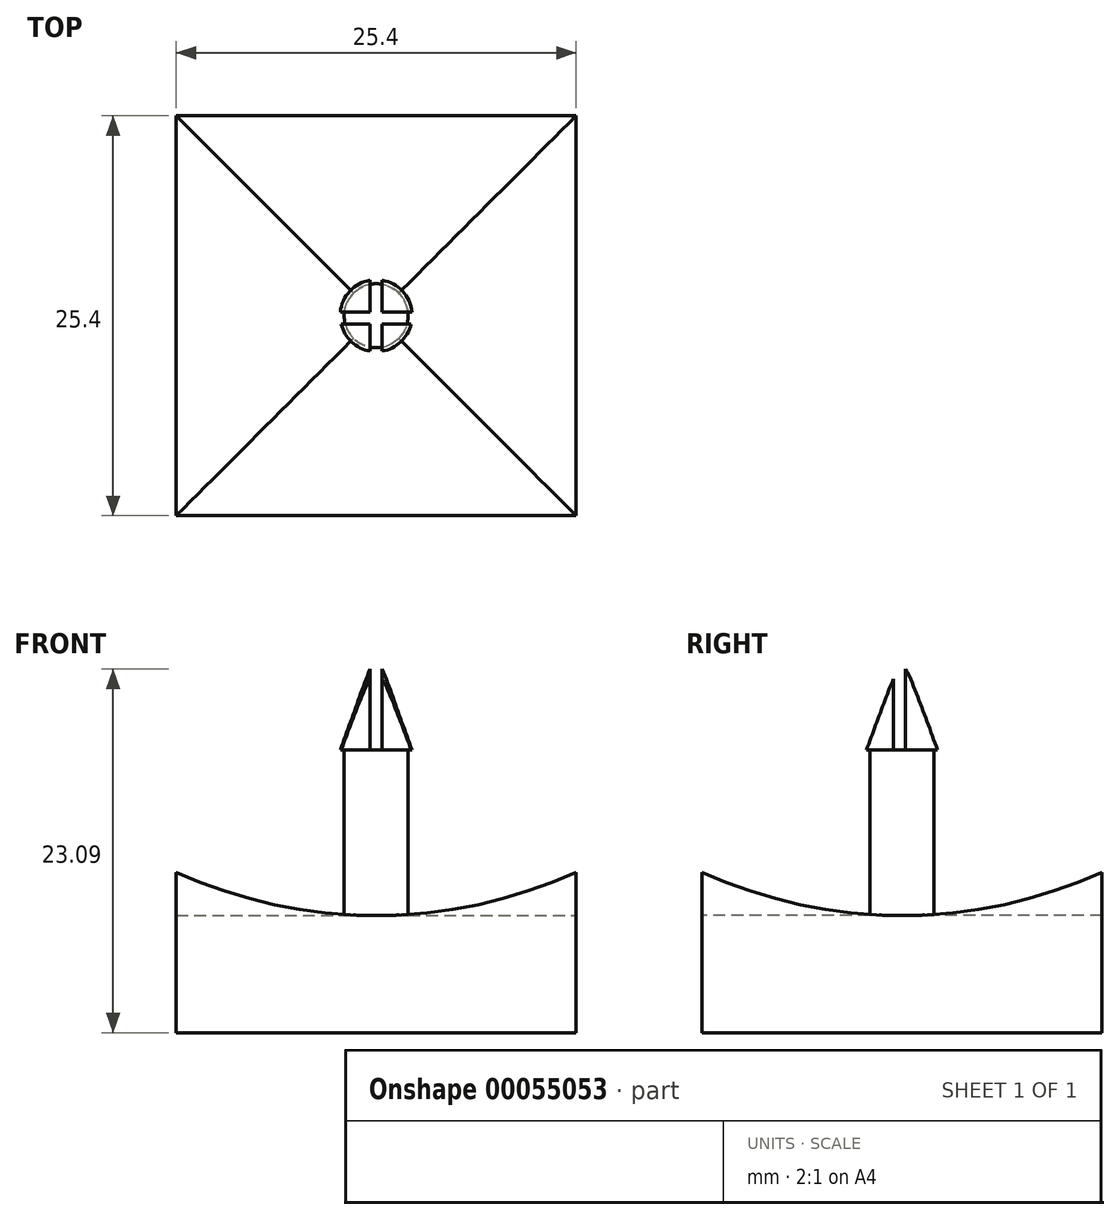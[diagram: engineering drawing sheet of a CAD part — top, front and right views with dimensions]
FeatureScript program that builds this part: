
annotation { "Feature Type Name" : "Feature", "Feature Type Description" : "" }
export const myFeature = defineFeature(function(context is Context, id is Id, definition is map)
    precondition{}
    {
        {
            var Q0;
            Q0=qCreatedBy(makeId("Top.planeOp"),FACE);
            var sketch = newSketch(context, id + "F0", { "sketchPlane" : qUnion([Q0])});
            skLineSegment(sketch, "E0.bottom", {"start": v(-12.7, 12.7) * mm, "end": v(12.7, 12.7) * mm});
            skLineSegment(sketch, "E0.top", {"start": v(-12.7, -12.7) * mm, "end": v(12.7, -12.7) * mm});
            skLineSegment(sketch, "E0.left", {"start": v(-12.7, 12.7) * mm, "end": v(-12.7, -12.7) * mm});
            skLineSegment(sketch, "E0.right", {"start": v(12.7, 12.7) * mm, "end": v(12.7, -12.7) * mm});
            skLineSegment(sketch, "E1", {"start": v(0, 12.7) * mm, "end": v(0, -12.7) * mm});
            skLineSegment(sketch, "E2", {"start": v(12.7, 0) * mm, "end": v(-12.7, 0) * mm});
            skPoint(sketch, "E3", {"position": v(0, 0) * mm});
            skSolve(sketch);
        }
        {
            var Q0;
            Q0 = qSketchRegion(id + "F0", true);
            extrude(context, id + "F1", {"entities" : qUnion([Q0]), "depth" : 12.7 * mm});
        }
        {
            var Q0;
            Q0=makeQuery(id+"F1.opExtrude","SWEPT_FACE",FACE,{"disambiguationData":[OSD([sQuery(id+"F0.wireOp",EDGE,"E0.top")])]});
            var sketch = newSketch(context, id + "F2", { "sketchPlane" : qUnion([Q0])});
            skLineSegment(sketch, "E4.bottom", {"start": v(-12.7, 0) * mm, "end": v(12.7, 0) * mm});
            skLineSegment(sketch, "E4.top", {"start": v(-12.7, 38.1) * mm, "end": v(12.7, 38.1) * mm});
            skLineSegment(sketch, "E4.left", {"start": v(-12.7, 0) * mm, "end": v(-12.7, 38.1) * mm});
            skLineSegment(sketch, "E4.right", {"start": v(12.7, 0) * mm, "end": v(12.7, 38.1) * mm});
            skPoint(sketch, "E5", {"position": v(0, 38.1) * mm});
            skCircle(sketch, "E6", {"center": v(0, 38.1) * mm, "radius": 30.66 * mm});
            skPoint(sketch, "E7", {"position": v(-12.7, 10.2) * mm});
            skSolve(sketch);
        }
        {
            var Q0;
            {var subQ3=sQuery(id+"F2.wireOp",EDGE,"E4.top");Q0=makeQuery(id+"F2.imprint","IMPRINT",FACE,{"disambiguationData":[TD([[makeQuery(id+"F2.imprint","IMPRINT",EDGE,{"derivedFrom":subQ3}),1.0]])]});}
            var Q1;
            {var subQ0=sQuery(id+"F2.wireOp",EDGE,"E4.top");Q1=makeQuery(id+"F2.imprint","IMPRINT",FACE,{"disambiguationData":[TD([[makeQuery(id+"F2.imprint","IMPRINT",EDGE,{"derivedFrom":subQ0}),-1.0]])]});}
            var Q2;
            {var subQ1=makeQuery(id+"F1.opExtrude","CAP_EDGE",EDGE,{"disambiguationData":[OSD([sQuery(id+"F0.wireOp",EDGE,"E0.top")])],"isStart":false});Q2=makeQuery(id+"F2.imprint","IMPRINT",FACE,{"disambiguationData":[TD([[makeQuery(id+"F2.imprint","IMPRINT",EDGE,{"derivedFrom":subQ1}),-1.0]])]});}
            extrude(context, id + "F3", {"entities" : qUnion([Q0, Q1, Q2]), "operationType" : NewBodyOperationType.REMOVE, "oppositeDirection" : true, "depth" : 25.4 * mm});
        }
        {
            var Q0;
            Q0=makeQuery(id+"F1.opExtrude","SWEPT_FACE",FACE,{"disambiguationData":[OSD([sQuery(id+"F0.wireOp",EDGE,"E0.right")])]});
            var sketch = newSketch(context, id + "F4", { "sketchPlane" : qUnion([Q0])});
            skLineSegment(sketch, "E8.bottom", {"start": v(-12.7, 0) * mm, "end": v(12.7, 0) * mm});
            skLineSegment(sketch, "E8.top", {"start": v(-12.7, 38.1) * mm, "end": v(12.7, 38.1) * mm});
            skLineSegment(sketch, "E8.left", {"start": v(-12.7, 0) * mm, "end": v(-12.7, 38.1) * mm});
            skLineSegment(sketch, "E8.right", {"start": v(12.7, 0) * mm, "end": v(12.7, 38.1) * mm});
            skPoint(sketch, "E9", {"position": v(0, 38.1) * mm});
            skCircle(sketch, "E10", {"center": v(0, 38.1) * mm, "radius": 30.66 * mm});
            skLineSegment(sketch, "E11", {"start": v(-12.7, 10.2) * mm, "end": v(0, 38.1) * mm});
            skLineSegment(sketch, "E12", {"start": v(12.7, 10.2) * mm, "end": v(0, 38.1) * mm});
            skLineSegment(sketch, "E13", {"start": v(0, 7.44) * mm, "end": v(0, 0) * mm});
            skSolve(sketch);
        }
        {
            var Q0;
            {var subQ0=sQuery(id+"F4.wireOp",EDGE,"E8.top");Q0=makeQuery(id+"F4.imprint","IMPRINT",FACE,{"disambiguationData":[TD([[makeQuery(id+"F4.imprint","IMPRINT",EDGE,{"derivedFrom":subQ0}),-1.0]])]});}
            var Q1;
            {var subQ1=makeQuery(id+"F3.boolean.opBoolean","INTERSECT",EDGE,{"derivedFrom":[makeQuery(id+"F1.opExtrude","SWEPT_FACE",FACE,{"disambiguationData":[OSD([sQuery(id+"F0.wireOp",EDGE,"E0.right")])]}),makeQuery(id+"F3.opExtrude","SWEPT_FACE",FACE,{"disambiguationData":[OSD([sQuery(id+"F2.wireOp",EDGE,"E6")])]})]});Q1=makeQuery(id+"F4.imprint","IMPRINT",FACE,{"disambiguationData":[TD([[makeQuery(id+"F4.imprint","IMPRINT",EDGE,{"derivedFrom":subQ1}),-1.0]])]});}
            extrude(context, id + "F5", {"entities" : qUnion([Q0, Q1]), "operationType" : NewBodyOperationType.REMOVE, "oppositeDirection" : true, "depth" : 25.4 * mm});
        }
        {
            var Q0;
            Q0=makeQuery(id+"F1.opExtrude","CAP_FACE",FACE,{"disambiguationData":[OSD([sQuery(id+"F0.wireOp",EDGE,"E0.bottom"),sQuery(id+"F0.wireOp",EDGE,"E0.top"),sQuery(id+"F0.wireOp",EDGE,"E0.left"),sQuery(id+"F0.wireOp",EDGE,"E0.right")])],"isStart":true});
            cPlane(context, id + "F6", {"entities" : qUnion([Q0]), "cplaneType" : CPlaneType.OFFSET, "offset" : 5.26 * mm, "oppositeDirection" : true, "width" : 152.4 * mm, "height" : 152.4 * mm});
        }
        {
            var Q0;
            Q0=makeQuery(id+"F1.opExtrude","SWEPT_FACE",FACE,{"disambiguationData":[OSD([sQuery(id+"F0.wireOp",EDGE,"E0.top")])]});
            cPlane(context, id + "F7", {"entities" : qUnion([Q0]), "cplaneType" : CPlaneType.OFFSET, "offset" : 12.7 * mm, "oppositeDirection" : true, "width" : 152.4 * mm, "height" : 152.4 * mm});
        }
        {
            var Q0;
            Q0=qCreatedBy(id+"F6.planeOp",FACE);
            var sketch = newSketch(context, id + "F8", { "sketchPlane" : qUnion([Q0])});
            skPoint(sketch, "E14", {"position": v(0, 0) * mm});
            skSolve(sketch);
        }
        {
            var Q0;
            Q0=qCreatedBy(id+"F7.planeOp",FACE);
            var sketch = newSketch(context, id + "F9", { "sketchPlane" : qUnion([Q0])});
            skPoint(sketch, "E15", {"position": v(0, 5.26) * mm});
            skLineSegment(sketch, "E16.bottom", {"start": v(2.03, 5.26) * mm, "end": v(0, 5.26) * mm});
            skLineSegment(sketch, "E16.top", {"start": v(2.03, 17.96) * mm, "end": v(0, 17.96) * mm});
            skLineSegment(sketch, "E16.left", {"start": v(2.03, 5.26) * mm, "end": v(2.03, 17.96) * mm});
            skLineSegment(sketch, "E16.right", {"start": v(0, 5.26) * mm, "end": v(0, 17.96) * mm});
            skLineSegment(sketch, "E17", {"start": v(0, 17.96) * mm, "end": v(0, 24.3) * mm});
            skLineSegment(sketch, "E18", {"start": v(0, 24.3) * mm, "end": v(2.29, 17.96) * mm});
            skLineSegment(sketch, "E19", {"start": v(2.29, 17.96) * mm, "end": v(2.03, 17.96) * mm});
            skSolve(sketch);
        }
        {
            var Q0;
            Q0=makeQuery(id+"F1.opExtrude","CAP_FACE",FACE,{"disambiguationData":[OSD([sQuery(id+"F0.wireOp",EDGE,"E0.bottom"),sQuery(id+"F0.wireOp",EDGE,"E0.top"),sQuery(id+"F0.wireOp",EDGE,"E0.left"),sQuery(id+"F0.wireOp",EDGE,"E0.right")])],"isStart":true});
            cPlane(context, id + "F10", {"entities" : qUnion([Q0]), "cplaneType" : CPlaneType.OFFSET, "offset" : 24.3 * mm, "oppositeDirection" : true, "width" : 152.4 * mm, "height" : 152.4 * mm});
        }
        {
            var Q0;
            Q0=qCreatedBy(id+"F10.planeOp",FACE);
            var sketch = newSketch(context, id + "F11", { "sketchPlane" : qUnion([Q0])});
            skPoint(sketch, "E20", {"position": v(0, 0) * mm});
            skLineSegment(sketch, "E21.bottom", {"start": v(0.38, 2.29) * mm, "end": v(-0.38, 2.29) * mm});
            skLineSegment(sketch, "E21.top", {"start": v(0.38, -2.29) * mm, "end": v(-0.38, -2.29) * mm});
            skLineSegment(sketch, "E21.left", {"start": v(0.38, 2.29) * mm, "end": v(0.38, -2.29) * mm});
            skLineSegment(sketch, "E21.right", {"start": v(-0.38, 2.29) * mm, "end": v(-0.38, -2.29) * mm});
            skLineSegment(sketch, "E22", {"start": v(0.38, 0) * mm, "end": v(-0.38, 0) * mm});
            skLineSegment(sketch, "E23.bottom", {"start": v(-2.29, -0.22) * mm, "end": v(2.29, -0.22) * mm});
            skLineSegment(sketch, "E23.top", {"start": v(-2.29, 0.54) * mm, "end": v(2.29, 0.54) * mm});
            skLineSegment(sketch, "E23.left", {"start": v(-2.29, -0.22) * mm, "end": v(-2.29, 0.54) * mm});
            skLineSegment(sketch, "E23.right", {"start": v(2.29, -0.22) * mm, "end": v(2.29, 0.54) * mm});
            skLineSegment(sketch, "E24", {"start": v(0, 0.54) * mm, "end": v(0, -0.22) * mm});
            skSolve(sketch);
        }
        {
            var Q0;
            Q0=makeQuery(id+"F9.imprint","IMPRINT",FACE,{"disambiguationData":[TD([[makeQuery(id+"F9.imprint","IMPRINT",EDGE,{"derivedFrom":sQuery(id+"F9.wireOp",EDGE,"E16.top")}),-1.0]])]});
            var Q1;
            Q1=makeQuery(id+"F9.imprint","IMPRINT",FACE,{"disambiguationData":[TD([[makeQuery(id+"F9.imprint","IMPRINT",EDGE,{"derivedFrom":sQuery(id+"F9.wireOp",EDGE,"E16.bottom")}),-1.0]])]});
            var Q2;
            Q2=sQuery(id+"F9.wireOp",EDGE,"E16.right");
            revolve(context, id + "F12", {"operationType" : NewBodyOperationType.ADD, "entities" : qUnion([Q0, Q1]), "axis" : qUnion([Q2]), "revolveType" : RevolveType.FULL});
        }
        {
            var Q0;
            Q0 = qSketchRegion(id + "F11", true);
            extrude(context, id + "F13", {"entities" : qUnion([Q0]), "operationType" : NewBodyOperationType.REMOVE, "depth" : 6.35 * mm});
        }
    });
